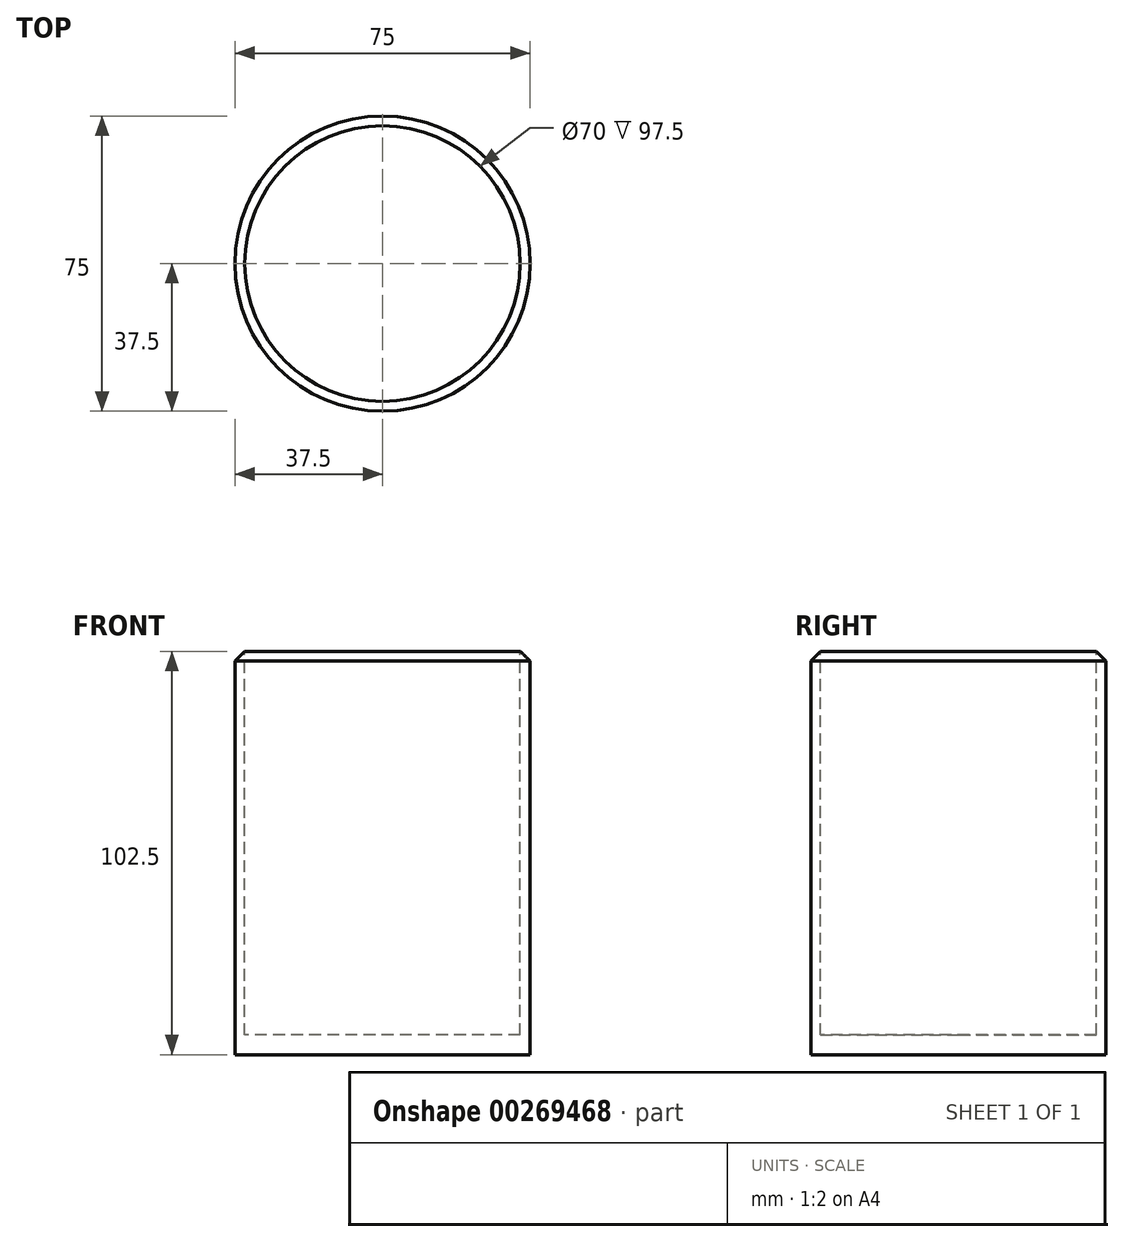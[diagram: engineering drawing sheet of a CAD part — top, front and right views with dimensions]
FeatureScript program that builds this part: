
annotation { "Feature Type Name" : "Feature", "Feature Type Description" : "" }
export const myFeature = defineFeature(function(context is Context, id is Id, definition is map)
    precondition{}
    {
        {
            var Q0;
            Q0=qCreatedBy(makeId("Top.planeOp"),FACE);
            var sketch = newSketch(context, id + "F0", { "sketchPlane" : qUnion([Q0])});
            skCircle(sketch, "E0", {"center": v(0, 0) * mm, "radius": 37.5 * mm});
            skLineSegment(sketch, "E1", {"start": v(0, 37.5) * mm, "end": v(0, -37.5) * mm, "construction": true});
            skCircle(sketch, "E2", {"center": v(0, 0) * mm, "radius": 35 * mm, "construction": true});
            skSolve(sketch);
        }
        {
            var Q0;
            Q0 = qSketchRegion(id + "F0", true);
            extrude(context, id + "F1", {"entities" : qUnion([Q0]), "depth" : 105 * mm});
        }
        {
            var Q0;
            Q0=makeQuery(id+"F1.opExtrude","CAP_FACE",FACE,{"disambiguationData":[OSD([sQuery(id+"F0.wireOp",EDGE,"E0")])],"isStart":false});
            var sketch = newSketch(context, id + "F2", { "sketchPlane" : qUnion([Q0])});
            skCircle(sketch, "E3", {"center": v(0, 0) * mm, "radius": 35 * mm});
            skSolve(sketch);
        }
        {
            var Q0;
            Q0 = qSketchRegion(id + "F2", true);
            extrude(context, id + "F3", {"entities" : qUnion([Q0]), "operationType" : NewBodyOperationType.REMOVE, "oppositeDirection" : true, "depth" : 100 * mm});
        }
        {
            var Q0;
            Q0=makeQuery(id+"F1.opExtrude","CAP_EDGE",EDGE,{"disambiguationData":[OSD([sQuery(id+"F0.wireOp",EDGE,"E0")])],"isStart":false});
            chamfer(context, id + "F4", {"entities" : qUnion([Q0]), "width" : 5 * mm, "tangentPropagation" : true});
        }
    });
